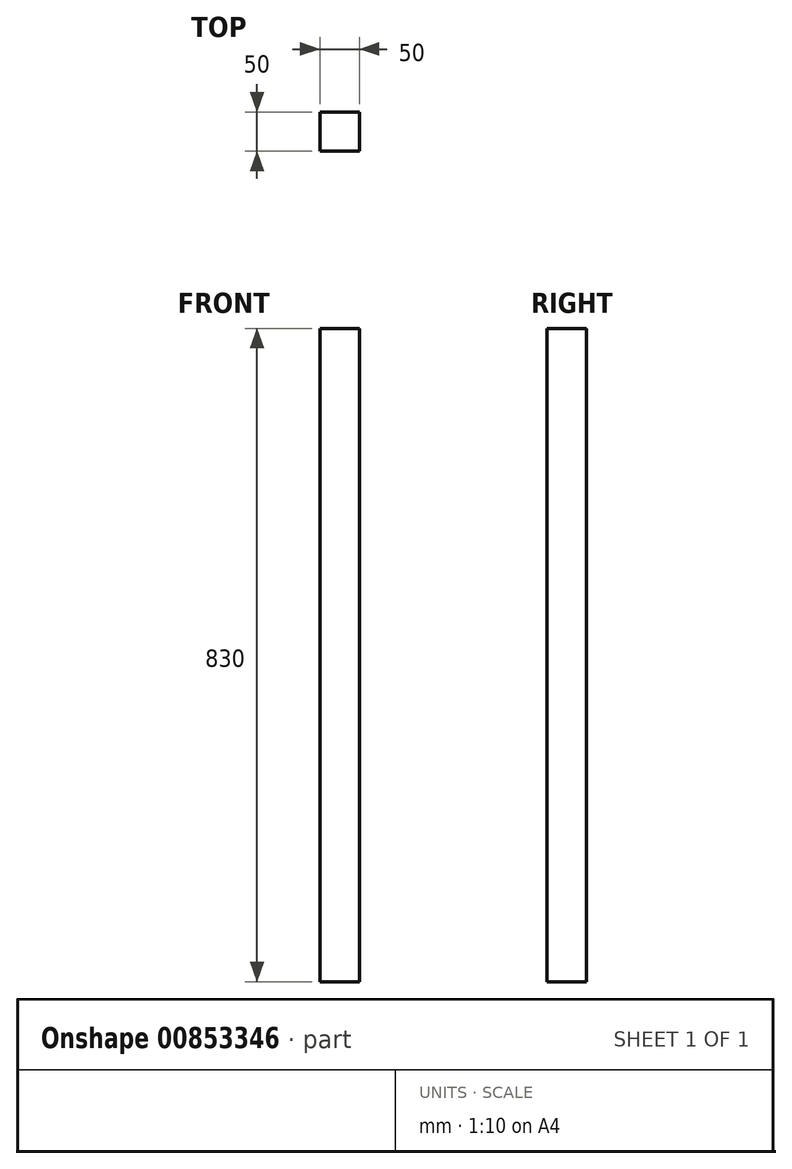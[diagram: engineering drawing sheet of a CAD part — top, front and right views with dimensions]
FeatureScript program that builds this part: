
annotation { "Feature Type Name" : "Feature", "Feature Type Description" : "" }
export const myFeature = defineFeature(function(context is Context, id is Id, definition is map)
    precondition{}
    {
        {
            var Q0;
            Q0=qCreatedBy(makeId("Top.planeOp"),FACE);
            var sketch = newSketch(context, id + "F0", { "sketchPlane" : qUnion([Q0])});
            skLineSegment(sketch, "E0", {"start": v(-17.78, 0) * mm, "end": v(32.22, 0) * mm});
            skLineSegment(sketch, "E1", {"start": v(-17.78, 0) * mm, "end": v(-17.78, -50) * mm});
            skLineSegment(sketch, "E2", {"start": v(32.22, 0) * mm, "end": v(32.22, -50) * mm});
            skLineSegment(sketch, "E3", {"start": v(32.22, -50) * mm, "end": v(-17.78, -50) * mm});
            skSolve(sketch);
        }
        {
            var Q0;
            Q0=makeQuery(id+"F0.imprint","IMPRINT",FACE,{"disambiguationData":[TD([[makeQuery(id+"F0.imprint","IMPRINT",EDGE,{"derivedFrom":sQuery(id+"F0.wireOp",EDGE,"E0")}),-1.0]])]});
            extrude(context, id + "F1", {"entities" : qUnion([Q0]), "depth" : 830 * mm, "offsetDistance" : 25 * mm});
        }
    });
